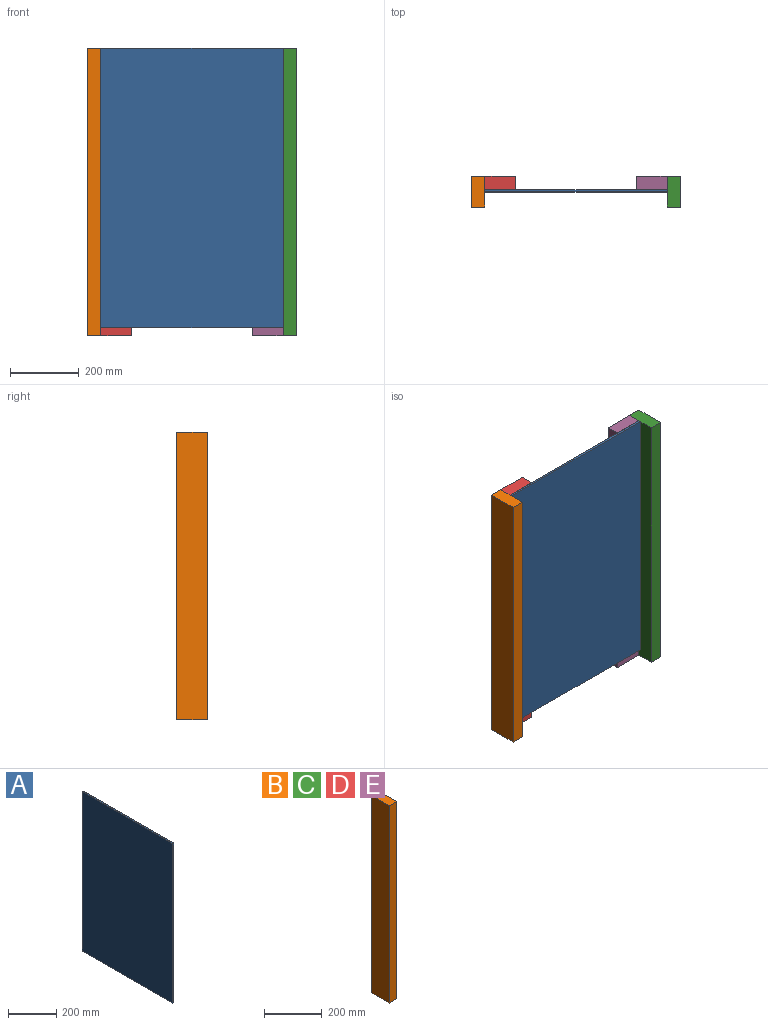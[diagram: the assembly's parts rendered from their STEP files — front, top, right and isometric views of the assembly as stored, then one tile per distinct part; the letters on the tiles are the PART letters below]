
ASSEMBLY  parts=5 mates=12
PART A: 6 faces, bbox 6.4x530.4x812.8 mm
  f0: plane 812.8x6.35mm, normal (0,-1,0), area 5161.3mm2, adj f1,f3,f4,f5
  f1: plane 812.8x530.35mm, normal (1,0,0), area 431070.1mm2, adj f0,f2,f4,f5
  f2: plane 812.8x6.35mm, normal (0,1,0), area 5161.3mm2, adj f1,f3,f4,f5
  f3: plane 812.8x530.35mm, normal (-1,0,0), area 431070.1mm2, adj f0,f2,f4,f5
  f4: plane 530.35x6.35mm, normal (0,0,1), area 3367.7mm2, adj f0,f1,f2,f3
  f5: plane 530.35x6.35mm, normal (0,0,-1), area 3367.7mm2, adj f0,f1,f2,f3
PART B: 6 faces, bbox 38.1x88.9x835.7 mm
  f0: plane 835.66x88.9mm, normal (1,0,0), area 74290.2mm2, adj f1,f3,f4,f5
  f1: plane 835.66x38.1mm, normal (0,1,0), area 31838.6mm2, adj f0,f2,f4,f5
  f2: plane 835.66x88.9mm, normal (-1,0,0), area 74290.2mm2, adj f1,f3,f4,f5
  f3: plane 835.66x38.1mm, normal (0,-1,0), area 31838.6mm2, adj f0,f2,f4,f5
  f4: plane 88.9x38.1mm, normal (0,0,1), area 3387.1mm2, adj f0,f1,f2,f3
  f5: plane 88.9x38.1mm, normal (0,0,-1), area 3387.1mm2, adj f0,f1,f2,f3
PART C: same geometry as B
PART D: same geometry as B
PART E: same geometry as B
PLACE A rot(axis=(0,0,1),90deg) t=(530.35,-38.1,22.86)mm
PLACE B at identity
PLACE C rot(axis=(0,0,1),180deg) t=(530.35,-88.9,0)mm
PLACE D rot(axis=(0.71,0.71,0),180deg) t=(88.9,0,835.66)mm
PLACE E rot(axis=(0,0,1),90deg) t=(441.45,0,0)mm
MATE planar A.f1 <-> D.f2  axis (0,1,0) through (265.18,-38.1,429.26)mm
MATE planar E.f4 <-> C.f4  axis (0,0,1) through (485.9,-19.05,835.66)mm
MATE planar A.f4 <-> D.f5  axis (0,0,1) through (265.18,-41.28,835.66)mm
MATE planar D.f3 <-> B.f0  axis (-1,0,0) through (0,-19.05,417.83)mm
MATE planar E.f0 <-> C.f3  axis (0,1,0) through (485.9,0,417.83)mm
MATE planar C.f0 <-> A.f0  axis (-1,0,0) through (530.35,-88.9,835.66)mm
MATE planar C.f4 <-> A.f4  axis (0,0,1) through (549.4,-44.45,835.66)mm
MATE planar A.f2 <-> B.f0  axis (-1,0,0) through (0,-41.28,429.26)mm
MATE planar C.f0 <-> E.f3  axis (-1,0,0) through (530.35,-44.45,417.83)mm
MATE planar D.f0 <-> B.f1  axis (0,1,0) through (44.45,0,417.83)mm
MATE planar E.f2 <-> A.f1  axis (0,-1,0) through (485.9,-38.1,417.83)mm
MATE planar D.f5 <-> B.f4  axis (0,0,1) through (44.45,-19.05,835.66)mm
